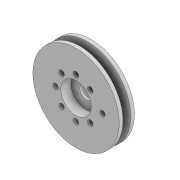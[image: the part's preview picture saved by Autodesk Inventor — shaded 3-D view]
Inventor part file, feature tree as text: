
AUTODESK INVENTOR PART (.ipt)
format: ipt  version: 2022 (Build 260153000, 153)  size: 371,200 bytes
history: native  units: mm
features: extrude x10, sketch x10, projected_geometry x5, thicken_offset x4, fillet x2, revolve x1, pattern_circular x1
ambient origin geometry x8: Origin, YZ Plane, XZ Plane, XY Plane, X Axis, Y Axis, Z Axis, Center Point
bodies: Solid1 (feature_tree)
feature tree (33):
  revolve  "Revolution1"  [1 undecoded]
  extrude  "Extrusion1"  Depth=1.5mm
  pattern_circular  "Circular Pattern1"  Count=10  [1 undecoded]
  extrude  "Extrusion2"  Depth=2.0mm
  extrude  "Extrusion3"  Depth=100.0mm TaperAngle=0.0deg
  extrude  "Extrusion8"  Depth=1.0mm TaperAngle=0.0deg
  extrude  "Extrusion6"  Depth=1.0mm
  extrude  "Extrusion7"  Depth=1.0mm TaperAngle=0.0deg
  sketch  "Sketch11"  dims[d16=10.5mm d17=100.0mm d18=0.0mm]
  extrude  "Extrusion10"  Depth=1.0mm
  extrude  "Extrusion11"  Depth=1.0mm TaperAngle=0.0deg
  thicken_offset  "Thicken1"
  thicken_offset  "Thicken2"
  thicken_offset  "Thicken3"
  fillet  "Fillet1"  Radius=18.0mm
  thicken_offset  "Thicken4"
  fillet  "Fillet2"  Radius=1.5mm
  extrude  "Extrusion12"  Depth=1.0mm
  extrude  "Extrusion9"  Depth=1.0mm TaperAngle=0.0deg
  sketch  "Sketch1"  dims[d0=6.0mm d1=3.0mm]
  sketch  "Sketch2"  dims[d2=14.0mm d4=1.5mm]
  sketch  "Sketch3"  dims[d5=1.5mm]
  sketch  "Sketch4"  dims[d6=360.0deg]
  projected_geometry  "Projected Loop1"
  projected_geometry  "Projected Loop2"
  sketch  "Sketch7"  dims[d7=2.1mm]
  sketch  "Sketch8"  dims[d8=8.0mm]
  projected_geometry  "Projected Loop5"
  sketch  "Sketch9"  dims[d9=9.0mm d10=100.0mm d11=0.0mm]
  sketch  "Sketch10"  dims[d12=80.0mm d13=360.0deg d15=2.0mm]
  sketch  "Sketch12"  dims[d19=4.0mm d20=5.0mm d21=0.0mm d24=10.5mm d25=2.0mm d26=0.0mm d31=2.0mm d32=4.0mm d33=0.0mm d34=18.0mm d35=1.5mm d36=0.0mm d37=5.0mm d38=1.0mm d39=0.0mm d40=100.0mm d41=0.0mm d44=4.0mm d45=4.0mm d46=4.0mm d47=4.0mm d48=4.0mm d49=4.0mm d50=4.0mm d51=3.0mm d52=3.0mm d53=3.0mm d54=1.6mm d55=0.0mm d56=6.0mm d57=0.0mm d58=23.0mm d59=3.0mm d60=2.0mm d61=3.0mm d62=3.0mm d63=3.0mm d64=3.0mm d65=1.0mm d66=1.5mm d67=1.5mm d68=0.9mm d69=1.05mm d70=4.0mm d71=60.0mm d73=360.0deg d75=100.0mm d76=0.0mm d42=0.5mm d43=0.872665mm]
  projected_geometry  "Projected Loop6"
  projected_geometry  "Project Cut Edges1"
note: 2 required parameter values undecoded (feature->parameter linkage not recoverable at this tier; creation-order binding heuristic only, values carry confidence <= 0.55)